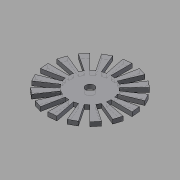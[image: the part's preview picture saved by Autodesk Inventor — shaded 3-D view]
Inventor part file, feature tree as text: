
AUTODESK INVENTOR PART (.ipt)
format: ipt  version: 2015 (Build 190159000, 159)  size: 173,568 bytes
history: native  units: in
note: dims shown in document units (in); Inventor stores cm internally (conversion verified against a paired STEP export)
features: other x3, sketch x1
ambient origin geometry x8: Origin, YZ Plane, XZ Plane, XY Plane, X Axis, Y Axis, Z Axis, Center Point
bodies: Solid1 (feature_tree)
feature tree (4):
  other  "encoder_MIR3.ipt"
  other  "Solid1::encoder_MIR3.ipt"
  other  "TaggingFeature1"
  sketch  "Sketch1"  dims[d0=0.3937in]
